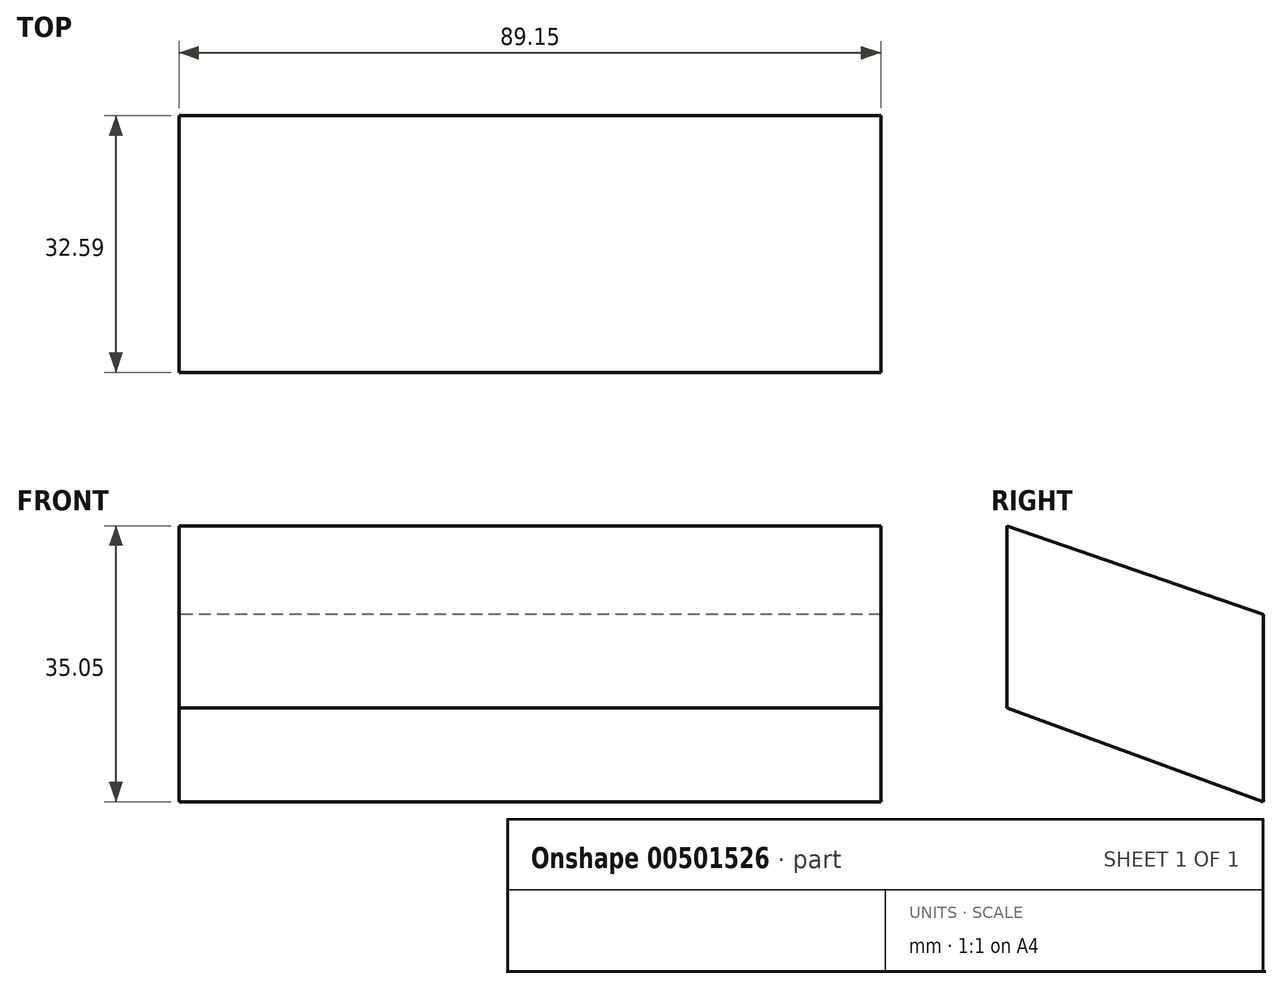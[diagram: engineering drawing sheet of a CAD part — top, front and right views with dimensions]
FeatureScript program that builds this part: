
annotation { "Feature Type Name" : "Feature", "Feature Type Description" : "" }
export const myFeature = defineFeature(function(context is Context, id is Id, definition is map)
    precondition{}
    {
        {
            var Q0;
            Q0=qCreatedBy(makeId("Right.planeOp"),FACE);
            var sketch = newSketch(context, id + "F0", { "sketchPlane" : qUnion([Q0])});
            skLineSegment(sketch, "E0", {"start": v(0, 0) * mm, "end": v(0, 23.11) * mm});
            skLineSegment(sketch, "E1", {"start": v(0, 23.11) * mm, "end": v(32.59, 11.82) * mm});
            skLineSegment(sketch, "E2", {"start": v(32.59, 11.82) * mm, "end": v(32.59, -11.94) * mm});
            skLineSegment(sketch, "E3", {"start": v(32.59, -11.94) * mm, "end": v(0, 0) * mm});
            skSolve(sketch);
        }
        {
            var Q0;
            Q0=makeQuery(id+"F0.imprint","IMPRINT",FACE,{"disambiguationData":[TD([[makeQuery(id+"F0.imprint","IMPRINT",EDGE,{"derivedFrom":sQuery(id+"F0.wireOp",EDGE,"E0")}),-1.0]])]});
            extrude(context, id + "F1", {"entities" : qUnion([Q0]), "depth" : 89.15 * mm});
        }
    });
